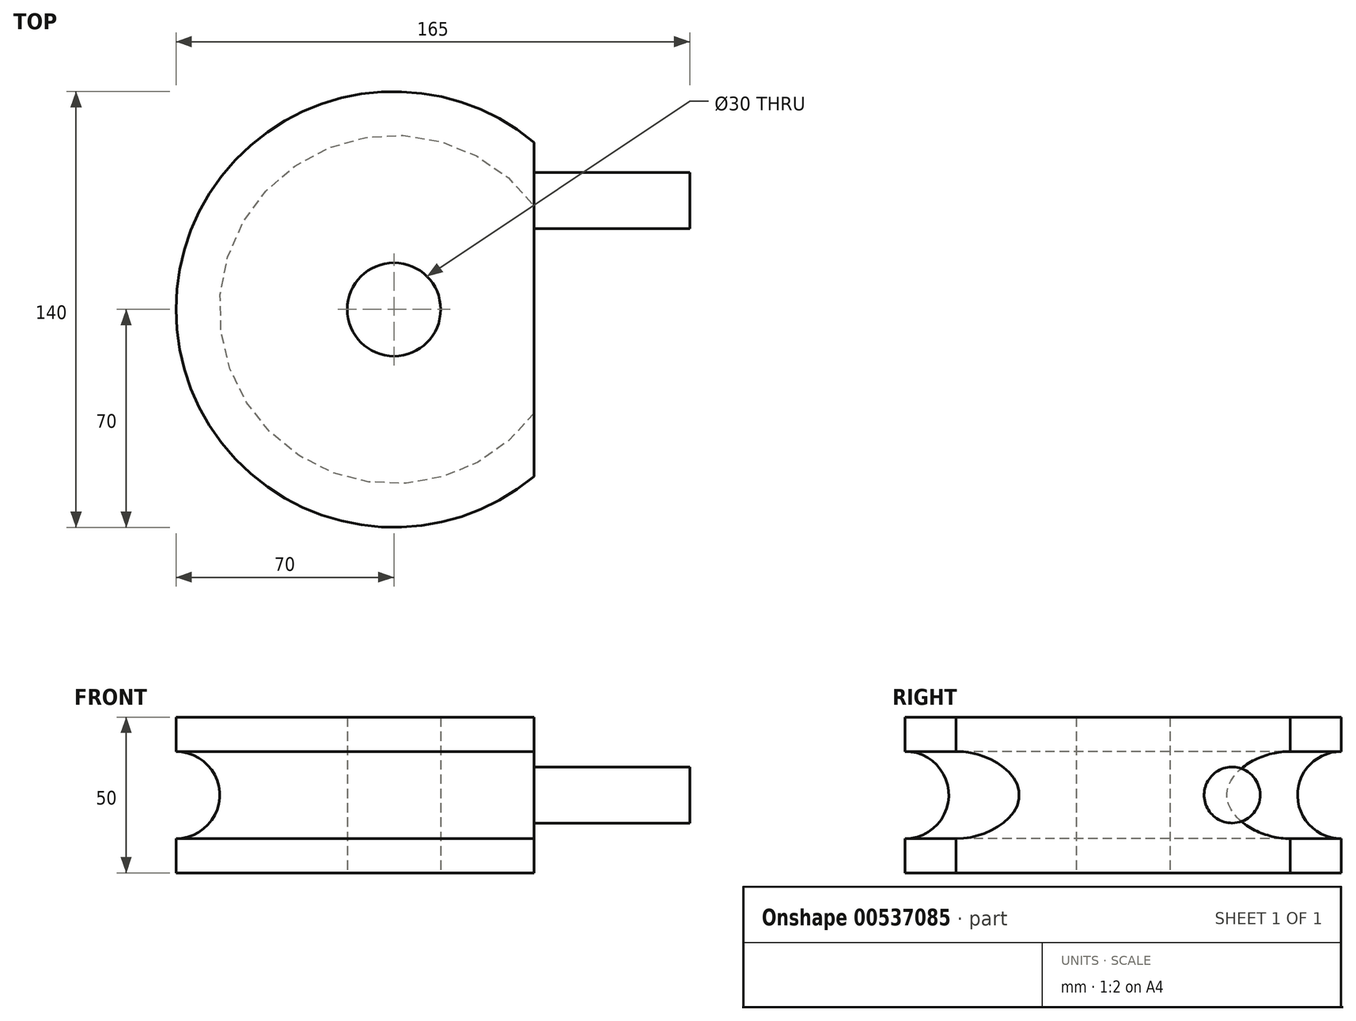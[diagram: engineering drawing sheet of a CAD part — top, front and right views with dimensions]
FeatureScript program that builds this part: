
annotation { "Feature Type Name" : "Feature", "Feature Type Description" : "" }
export const myFeature = defineFeature(function(context is Context, id is Id, definition is map)
    precondition{}
    {
        {
            var Q0;
            Q0=qCreatedBy(makeId("Top.planeOp"),FACE);
            var sketch = newSketch(context, id + "F0", { "sketchPlane" : qUnion([Q0])});
            skCircle(sketch, "E0", {"center": v(0, 0) * mm, "radius": 70 * mm});
            skLineSegment(sketch, "E1", {"start": v(45, 53.62) * mm, "end": v(45, -53.62) * mm});
            skCircle(sketch, "E2", {"center": v(0, 0) * mm, "radius": 15 * mm});
            skSolve(sketch);
        }
        {
            var Q0;
            {var subQ0=sQuery(id+"F0.wireOp",EDGE,"E1");Q0=makeQuery(id+"F0.imprint","IMPRINT",FACE,{"disambiguationData":[TD([[makeQuery(id+"F0.imprint","IMPRINT",EDGE,{"derivedFrom":subQ0}),-1.0]])]});}
            extrude(context, id + "F1", {"entities" : qUnion([Q0]), "endBound" : BoundingType.SYMMETRIC, "depth" : 50 * mm, "offsetDistance" : 25 * mm});
        }
        {
            var Q0;
            Q0=qCreatedBy(makeId("Right.planeOp"),FACE);
            var sketch = newSketch(context, id + "F2", { "sketchPlane" : qUnion([Q0])});
            skLineSegment(sketch, "E3", {"start": v(70, 25) * mm, "end": v(70, -25) * mm});
            skLineSegment(sketch, "E4", {"start": v(70, 25) * mm, "end": v(70, -25) * mm, "construction": true});
            skCircle(sketch, "E5", {"center": v(70, 0) * mm, "radius": 14 * mm});
            skSolve(sketch);
        }
        {
            var Q0;
            {var subQ0=sQuery(id+"F2.wireOp",EDGE,"E5");var subQ1=sQuery(id+"F2.wireOp",EDGE,"E3");var subQ2=makeQuery(id+"F2.imprint","INTERSECT",VERTEX,{"disambiguationData":[OD(0.0)],"derivedFrom":[subQ1,subQ0]});Q0=makeQuery(id+"F2.imprint","IMPRINT",FACE,{"disambiguationData":[TD([[makeQuery(id+"F2.imprint","IMPRINT",EDGE,{"disambiguationData":[TD([[subQ2,1.0]])],"derivedFrom":subQ1}),-1.0]])]});}
            var Q1;
            Q1=makeQuery(id+"F1.opExtrude","CAP_EDGE",EDGE,{"disambiguationData":[OSD([sQuery(id+"F0.wireOp",EDGE,"E2")])],"isStart":false});
            revolve(context, id + "F3", {"operationType" : NewBodyOperationType.REMOVE, "entities" : qUnion([Q0]), "axis" : qUnion([Q1]), "revolveType" : RevolveType.FULL, "oppositeDirection" : true});
        }
        {
            var Q0;
            Q0=makeQuery(id+"F1.opExtrude","SWEPT_FACE",FACE,{"disambiguationData":[OSD([sQuery(id+"F0.wireOp",EDGE,"E1")])]});
            var sketch = newSketch(context, id + "F4", { "sketchPlane" : qUnion([Q0])});
            skCircle(sketch, "E6", {"center": v(35, 0) * mm, "radius": 9 * mm});
            skArc(sketch, "E7", {"start": v(59.8, 9.6) * mm, "mid": v(56, 0) * mm, "end": v(59.8, -9.6) * mm, "construction": true});
            skSolve(sketch);
        }
        {
            var Q0;
            Q0=makeQuery(id+"F4.imprint","IMPRINT",FACE,{"disambiguationData":[TD([[makeQuery(id+"F4.imprint","IMPRINT",EDGE,{"derivedFrom":sQuery(id+"F4.wireOp",EDGE,"E6")}),1.0]])]});
            extrude(context, id + "F5", {"entities" : qUnion([Q0]), "operationType" : NewBodyOperationType.ADD, "depth" : 50 * mm, "offsetDistance" : 25 * mm});
        }
    });
